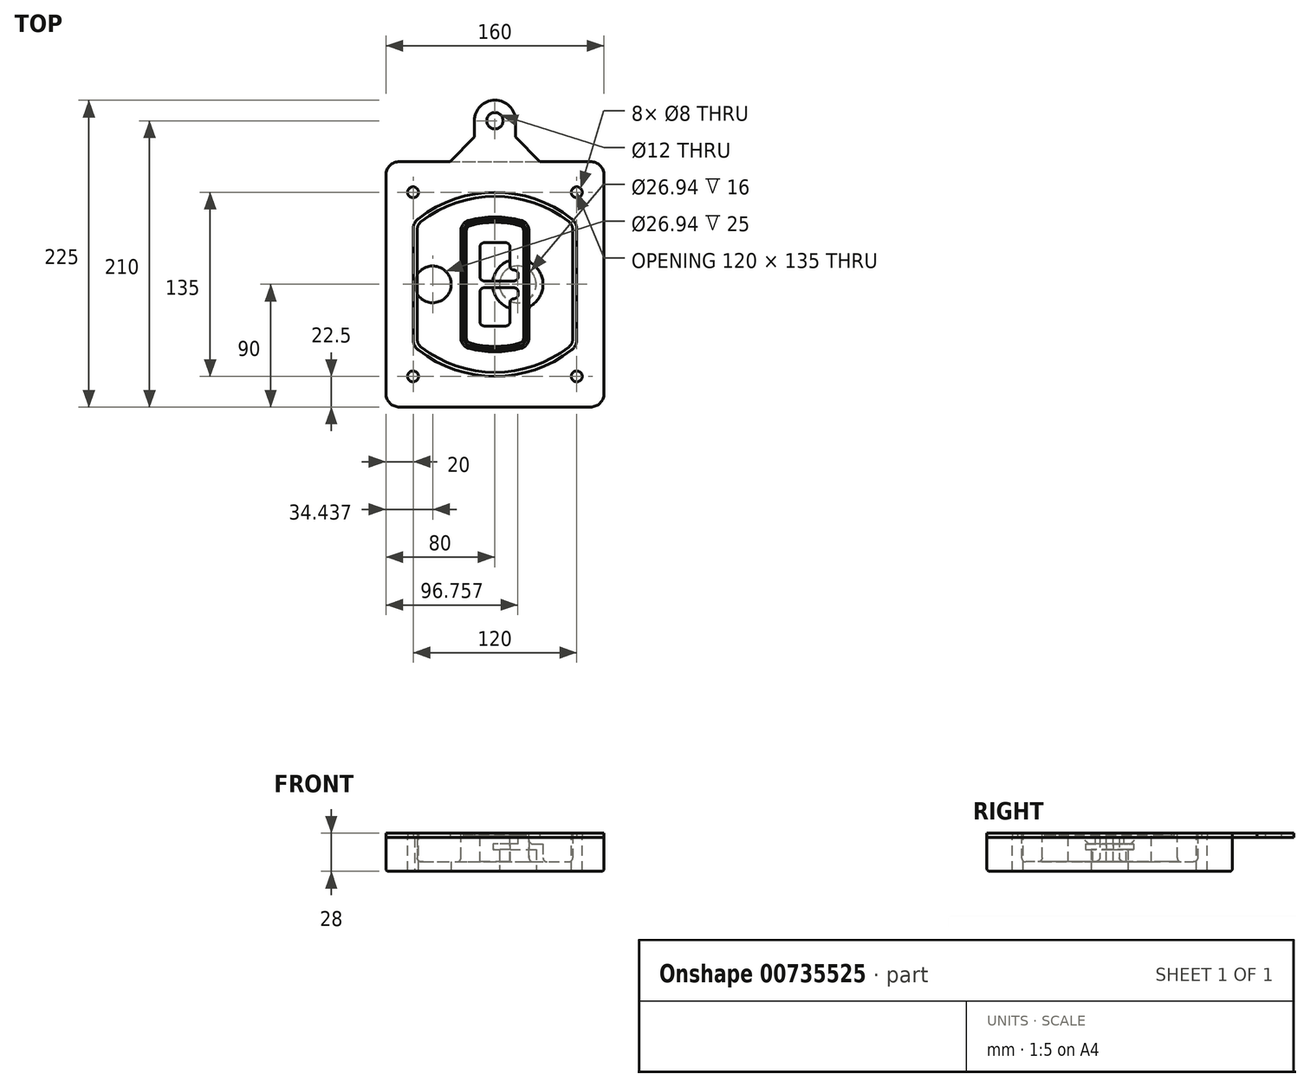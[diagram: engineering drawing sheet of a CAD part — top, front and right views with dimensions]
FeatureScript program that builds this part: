
annotation { "Feature Type Name" : "Feature", "Feature Type Description" : "" }
export const myFeature = defineFeature(function(context is Context, id is Id, definition is map)
    precondition{}
    {
        {
            var Q0;
            Q0=qCreatedBy(makeId("Top.planeOp"),FACE);
            var sketch = newSketch(context, id + "F0", { "sketchPlane" : qUnion([Q0])});
            skPoint(sketch, "E0.rect.middle", {"position": v(0, 0) * mm});
            skLineSegment(sketch, "E1.bottom", {"start": v(-70, -90) * mm, "end": v(70, -90) * mm});
            skLineSegment(sketch, "E1.top", {"start": v(-70, 90) * mm, "end": v(70, 90) * mm});
            skLineSegment(sketch, "E1.left", {"start": v(-80, -80) * mm, "end": v(-80, 80) * mm});
            skLineSegment(sketch, "E1.right", {"start": v(80, -80) * mm, "end": v(80, 80) * mm});
            skLineSegment(sketch, "E2", {"start": v(-80, 90) * mm, "end": v(80, -90) * mm, "construction": true});
            skLineSegment(sketch, "E3", {"start": v(80, 90) * mm, "end": v(-80, -90) * mm, "construction": true});
            skCircle(sketch, "E4", {"center": v(-60, 67.5) * mm, "radius": 4 * mm});
            skCircle(sketch, "E5", {"center": v(60, 67.5) * mm, "radius": 4 * mm});
            skCircle(sketch, "E6", {"center": v(60, -67.5) * mm, "radius": 4 * mm});
            skCircle(sketch, "E7", {"center": v(-60, -67.5) * mm, "radius": 4 * mm});
            skLineSegment(sketch, "E8", {"start": v(-60, 67.5) * mm, "end": v(60, 67.5) * mm, "construction": true});
            skLineSegment(sketch, "E9", {"start": v(60, 67.5) * mm, "end": v(60, -67.5) * mm, "construction": true});
            skLineSegment(sketch, "E10", {"start": v(60, -67.5) * mm, "end": v(-60, -67.5) * mm, "construction": true});
            skLineSegment(sketch, "E11", {"start": v(-60, -67.5) * mm, "end": v(-60, 67.5) * mm, "construction": true});
            skLineSegment(sketch, "E12", {"start": v(-60, 40.3) * mm, "end": v(-60, -40.3) * mm});
            skLineSegment(sketch, "E13", {"start": v(60, 40.3) * mm, "end": v(60, -40.3) * mm});
            skArc(sketch, "E14", {"start": v(56.15, 48.18) * mm, "mid": v(0, 67.5) * mm, "end": v(-56.15, 48.18) * mm});
            skArc(sketch, "E15", {"start": v(-56.15, -48.18) * mm, "mid": v(0, -67.5) * mm, "end": v(56.15, -48.18) * mm});
            skLineSegment(sketch, "E16", {"start": v(-60, 0) * mm, "end": v(60, 0) * mm, "construction": true});
            skPoint(sketch, "E17.visualSharp", {"position": v(-60, -45) * mm});
            skArc(sketch, "E17.filletArc", {"start": v(-60, -40.3) * mm, "mid": v(-58.99, -44.68) * mm, "end": v(-56.15, -48.18) * mm});
            skPoint(sketch, "E18.visualSharp", {"position": v(-60, 45) * mm});
            skArc(sketch, "E18.filletArc", {"start": v(-56.15, 48.18) * mm, "mid": v(-58.99, 44.68) * mm, "end": v(-60, 40.3) * mm});
            skPoint(sketch, "E19.visualSharp", {"position": v(60, 45) * mm});
            skArc(sketch, "E19.filletArc", {"start": v(60, 40.3) * mm, "mid": v(58.99, 44.68) * mm, "end": v(56.15, 48.18) * mm});
            skPoint(sketch, "E20.visualSharp", {"position": v(60, -45) * mm});
            skArc(sketch, "E20.filletArc", {"start": v(56.15, -48.18) * mm, "mid": v(58.99, -44.68) * mm, "end": v(60, -40.3) * mm});
            skPoint(sketch, "E21.visualSharp", {"position": v(-80, 90) * mm});
            skArc(sketch, "E21.filletArc", {"start": v(-70, 90) * mm, "mid": v(-77.07, 87.07) * mm, "end": v(-80, 80) * mm});
            skPoint(sketch, "E22.visualSharp", {"position": v(80, 90) * mm});
            skArc(sketch, "E22.filletArc", {"start": v(80, 80) * mm, "mid": v(77.07, 87.07) * mm, "end": v(70, 90) * mm});
            skPoint(sketch, "E23.visualSharp", {"position": v(80, -90) * mm});
            skArc(sketch, "E23.filletArc", {"start": v(70, -90) * mm, "mid": v(77.07, -87.07) * mm, "end": v(80, -80) * mm});
            skPoint(sketch, "E24.visualSharp", {"position": v(-80, -90) * mm});
            skArc(sketch, "E24.filletArc", {"start": v(-80, -80) * mm, "mid": v(-77.07, -87.07) * mm, "end": v(-70, -90) * mm});
            skArc(sketch, "E25.0", {"start": v(57, 40.3) * mm, "mid": v(56.3, 43.36) * mm, "end": v(54.3, 45.81) * mm});
            skLineSegment(sketch, "E25.1", {"start": v(57, 40.3) * mm, "end": v(57, -40.3) * mm});
            skArc(sketch, "E25.2", {"start": v(54.3, -45.81) * mm, "mid": v(56.3, -43.36) * mm, "end": v(57, -40.3) * mm});
            skArc(sketch, "E25.3", {"start": v(-54.3, -45.81) * mm, "mid": v(0, -64.5) * mm, "end": v(54.3, -45.81) * mm});
            skArc(sketch, "E25.4", {"start": v(-57, -40.3) * mm, "mid": v(-56.3, -43.36) * mm, "end": v(-54.3, -45.81) * mm});
            skArc(sketch, "E25.5", {"start": v(54.3, 45.81) * mm, "mid": v(0, 64.5) * mm, "end": v(-54.3, 45.81) * mm});
            skLineSegment(sketch, "E25.6", {"start": v(-57, 40.3) * mm, "end": v(-57, -40.3) * mm});
            skArc(sketch, "E25.7", {"start": v(-54.3, 45.81) * mm, "mid": v(-56.3, 43.36) * mm, "end": v(-57, 40.3) * mm});
            skArc(sketch, "E26.0", {"start": v(-58.62, 51.33) * mm, "mid": v(-62.58, 46.43) * mm, "end": v(-64, 40.3) * mm});
            skArc(sketch, "E26.1", {"start": v(58.62, 51.33) * mm, "mid": v(0, 71.5) * mm, "end": v(-58.62, 51.33) * mm});
            skArc(sketch, "E26.2", {"start": v(64, 40.3) * mm, "mid": v(62.58, 46.43) * mm, "end": v(58.62, 51.33) * mm});
            skLineSegment(sketch, "E26.3", {"start": v(64, 40.3) * mm, "end": v(64, -40.3) * mm});
            skArc(sketch, "E26.4", {"start": v(58.62, -51.33) * mm, "mid": v(62.58, -46.43) * mm, "end": v(64, -40.3) * mm});
            skLineSegment(sketch, "E26.5", {"start": v(-64, 40.3) * mm, "end": v(-64, -40.3) * mm});
            skArc(sketch, "E26.6", {"start": v(-58.62, -51.33) * mm, "mid": v(0, -71.5) * mm, "end": v(58.62, -51.33) * mm});
            skArc(sketch, "E26.7", {"start": v(-64, -40.3) * mm, "mid": v(-62.58, -46.43) * mm, "end": v(-58.62, -51.33) * mm});
            skSolve(sketch);
        }
        {
            var Q0;
            Q0=makeQuery(id+"F0.imprint","IMPRINT",FACE,{"disambiguationData":[TD([[makeQuery(id+"F0.imprint","IMPRINT",EDGE,{"derivedFrom":sQuery(id+"F0.wireOp",EDGE,"E1.bottom")}),1.0]])]});
            var Q1;
            Q1=makeQuery(id+"F0.imprint","IMPRINT",FACE,{"disambiguationData":[TD([[makeQuery(id+"F0.imprint","IMPRINT",EDGE,{"derivedFrom":sQuery(id+"F0.wireOp",EDGE,"E12")}),1.0]])]});
            var Q2;
            Q2=makeQuery(id+"F0.imprint","IMPRINT",FACE,{"disambiguationData":[TD([[makeQuery(id+"F0.imprint","IMPRINT",EDGE,{"derivedFrom":sQuery(id+"F0.wireOp",EDGE,"E25.0")}),1.0]])]});
            var Q3;
            Q3=makeQuery(id+"F0.imprint","IMPRINT",FACE,{"disambiguationData":[TD([[makeQuery(id+"F0.imprint","IMPRINT",EDGE,{"derivedFrom":sQuery(id+"F0.wireOp",EDGE,"E12")}),-1.0]])]});
            extrude(context, id + "F1", {"entities" : qUnion([Q0, Q1, Q2, Q3]), "oppositeDirection" : true, "depth" : 25 * mm, "offsetDistance" : 25 * mm});
        }
        {
            var Q0;
            Q0=makeQuery(id+"F0.imprint","IMPRINT",FACE,{"disambiguationData":[TD([[makeQuery(id+"F0.imprint","IMPRINT",EDGE,{"derivedFrom":sQuery(id+"F0.wireOp",EDGE,"E12")}),1.0]])]});
            extrude(context, id + "F2", {"entities" : qUnion([Q0]), "operationType" : NewBodyOperationType.ADD, "depth" : 3 * mm});
        }
        {
            var Q0;
            Q0=makeQuery(id+"F0.imprint","IMPRINT",FACE,{"disambiguationData":[TD([[makeQuery(id+"F0.imprint","IMPRINT",EDGE,{"derivedFrom":sQuery(id+"F0.wireOp",EDGE,"E25.0")}),1.0]])]});
            extrude(context, id + "F3", {"entities" : qUnion([Q0]), "operationType" : NewBodyOperationType.REMOVE, "oppositeDirection" : true, "depth" : 18 * mm});
        }
        {
            var Q0;
            Q0=makeQuery(id+"F2.opExtrude","CAP_FACE",FACE,{"disambiguationData":[OSD([sQuery(id+"F0.wireOp",EDGE,"E12"),sQuery(id+"F0.wireOp",EDGE,"E13"),sQuery(id+"F0.wireOp",EDGE,"E14"),sQuery(id+"F0.wireOp",EDGE,"E15"),sQuery(id+"F0.wireOp",EDGE,"E17.filletArc"),sQuery(id+"F0.wireOp",EDGE,"E18.filletArc"),sQuery(id+"F0.wireOp",EDGE,"E19.filletArc"),sQuery(id+"F0.wireOp",EDGE,"E20.filletArc"),sQuery(id+"F0.wireOp",EDGE,"E25.0"),sQuery(id+"F0.wireOp",EDGE,"E25.1"),sQuery(id+"F0.wireOp",EDGE,"E25.2"),sQuery(id+"F0.wireOp",EDGE,"E25.3"),sQuery(id+"F0.wireOp",EDGE,"E25.4"),sQuery(id+"F0.wireOp",EDGE,"E25.5"),sQuery(id+"F0.wireOp",EDGE,"E25.6"),sQuery(id+"F0.wireOp",EDGE,"E25.7")])],"isStart":false});
            var sketch = newSketch(context, id + "F4", { "sketchPlane" : qUnion([Q0])});
            skArc(sketch, "E27.0", {"start": v(-19.08, -46.97) * mm, "mid": v(0, -49.5) * mm, "end": v(19.08, -46.97) * mm});
            skArc(sketch, "E28.0", {"start": v(19.08, 46.97) * mm, "mid": v(0, 49.5) * mm, "end": v(-19.08, 46.97) * mm});
            skLineSegment(sketch, "E29", {"start": v(-25, 39.25) * mm, "end": v(-25, -39.25) * mm});
            skLineSegment(sketch, "E30", {"start": v(25, 39.25) * mm, "end": v(25, -39.25) * mm});
            skLineSegment(sketch, "E31", {"start": v(-25, 45.1) * mm, "end": v(25, 45.1) * mm, "construction": true});
            skLineSegment(sketch, "E32", {"start": v(-25, -45.1) * mm, "end": v(25, -45.1) * mm, "construction": true});
            skPoint(sketch, "E33.visualSharp", {"position": v(-25, 45.1) * mm});
            skArc(sketch, "E33.filletArc", {"start": v(-19.08, 46.97) * mm, "mid": v(-23.35, 44.11) * mm, "end": v(-25, 39.25) * mm});
            skPoint(sketch, "E34.visualSharp", {"position": v(25, 45.1) * mm});
            skArc(sketch, "E34.filletArc", {"start": v(25, 39.25) * mm, "mid": v(23.35, 44.11) * mm, "end": v(19.08, 46.97) * mm});
            skPoint(sketch, "E35.visualSharp", {"position": v(25, -45.1) * mm});
            skArc(sketch, "E35.filletArc", {"start": v(19.08, -46.97) * mm, "mid": v(23.35, -44.11) * mm, "end": v(25, -39.25) * mm});
            skPoint(sketch, "E36.visualSharp", {"position": v(-25, -45.1) * mm});
            skArc(sketch, "E36.filletArc", {"start": v(-25, -39.25) * mm, "mid": v(-23.35, -44.11) * mm, "end": v(-19.08, -46.97) * mm});
            skArc(sketch, "E37.0", {"start": v(54.3, 45.81) * mm, "mid": v(0, 64.5) * mm, "end": v(-54.3, 45.81) * mm});
            skArc(sketch, "E37.1", {"start": v(-54.3, 45.81) * mm, "mid": v(-56.3, 43.36) * mm, "end": v(-57, 40.3) * mm});
            skLineSegment(sketch, "E37.2", {"start": v(-57, 40.3) * mm, "end": v(-57, -40.3) * mm});
            skArc(sketch, "E37.3", {"start": v(-57, -40.3) * mm, "mid": v(-56.3, -43.36) * mm, "end": v(-54.3, -45.81) * mm});
            skArc(sketch, "E37.4", {"start": v(-54.3, -45.81) * mm, "mid": v(0, -64.5) * mm, "end": v(54.3, -45.81) * mm});
            skArc(sketch, "E37.5", {"start": v(54.3, -45.81) * mm, "mid": v(56.3, -43.36) * mm, "end": v(57, -40.3) * mm});
            skLineSegment(sketch, "E37.6", {"start": v(57, 40.3) * mm, "end": v(57, -40.3) * mm});
            skArc(sketch, "E37.7", {"start": v(57, 40.3) * mm, "mid": v(56.3, 43.36) * mm, "end": v(54.3, 45.81) * mm});
            skLineSegment(sketch, "E38.0", {"start": v(23, 39.25) * mm, "end": v(23, -39.25) * mm});
            skArc(sketch, "E38.1", {"start": v(18.56, -45.04) * mm, "mid": v(21.76, -42.9) * mm, "end": v(23, -39.25) * mm});
            skArc(sketch, "E38.2", {"start": v(-18.56, -45.04) * mm, "mid": v(0, -47.5) * mm, "end": v(18.56, -45.04) * mm});
            skArc(sketch, "E38.3", {"start": v(-23, -39.25) * mm, "mid": v(-21.76, -42.9) * mm, "end": v(-18.56, -45.04) * mm});
            skLineSegment(sketch, "E38.4", {"start": v(-23, 39.25) * mm, "end": v(-23, -39.25) * mm});
            skArc(sketch, "E38.5", {"start": v(23, 39.25) * mm, "mid": v(21.76, 42.9) * mm, "end": v(18.56, 45.04) * mm});
            skArc(sketch, "E38.6", {"start": v(-18.56, 45.04) * mm, "mid": v(-21.76, 42.9) * mm, "end": v(-23, 39.25) * mm});
            skArc(sketch, "E38.7", {"start": v(18.56, 45.04) * mm, "mid": v(0, 47.5) * mm, "end": v(-18.56, 45.04) * mm});
            skArc(sketch, "E39.0", {"start": v(21, 39.25) * mm, "mid": v(20.18, 41.68) * mm, "end": v(18.04, 43.1) * mm});
            skLineSegment(sketch, "E39.1", {"start": v(21, 39.25) * mm, "end": v(21, -39.25) * mm});
            skArc(sketch, "E39.2", {"start": v(18.04, -43.1) * mm, "mid": v(20.18, -41.68) * mm, "end": v(21, -39.25) * mm});
            skArc(sketch, "E39.3", {"start": v(-18.04, -43.1) * mm, "mid": v(0, -45.5) * mm, "end": v(18.04, -43.1) * mm});
            skArc(sketch, "E39.4", {"start": v(-21, -39.25) * mm, "mid": v(-20.18, -41.68) * mm, "end": v(-18.04, -43.1) * mm});
            skArc(sketch, "E39.5", {"start": v(18.04, 43.1) * mm, "mid": v(0, 45.5) * mm, "end": v(-18.04, 43.1) * mm});
            skLineSegment(sketch, "E39.6", {"start": v(-21, 39.25) * mm, "end": v(-21, -39.25) * mm});
            skArc(sketch, "E39.7", {"start": v(-18.04, 43.1) * mm, "mid": v(-20.18, 41.68) * mm, "end": v(-21, 39.25) * mm});
            skLineSegment(sketch, "E40", {"start": v(-25, 0) * mm, "end": v(25, 0) * mm, "construction": true});
            skLineSegment(sketch, "E41", {"start": v(-11, 5.5) * mm, "end": v(-11, 27.5) * mm});
            skLineSegment(sketch, "E42", {"start": v(-8, 30.5) * mm, "end": v(8, 30.5) * mm});
            skLineSegment(sketch, "E43", {"start": v(11, 27.5) * mm, "end": v(11, 13.5) * mm});
            skLineSegment(sketch, "E44", {"start": v(14, 10.5) * mm, "end": v(14, 10.5) * mm});
            skLineSegment(sketch, "E45", {"start": v(17, 7.5) * mm, "end": v(17, 5.5) * mm});
            skLineSegment(sketch, "E46", {"start": v(14, 2.5) * mm, "end": v(-8, 2.5) * mm});
            skPoint(sketch, "E47.visualSharp", {"position": v(-11, 30.5) * mm});
            skArc(sketch, "E47.filletArc", {"start": v(-8, 30.5) * mm, "mid": v(-10.12, 29.62) * mm, "end": v(-11, 27.5) * mm});
            skPoint(sketch, "E48.visualSharp", {"position": v(11, 30.5) * mm});
            skArc(sketch, "E48.filletArc", {"start": v(11, 27.5) * mm, "mid": v(10.12, 29.62) * mm, "end": v(8, 30.5) * mm});
            skPoint(sketch, "E49.visualSharp", {"position": v(11, 10.5) * mm});
            skArc(sketch, "E49.filletArc", {"start": v(11, 13.5) * mm, "mid": v(11.88, 11.38) * mm, "end": v(14, 10.5) * mm});
            skPoint(sketch, "E50.visualSharp", {"position": v(17, 10.5) * mm});
            skArc(sketch, "E50.filletArc", {"start": v(17, 7.5) * mm, "mid": v(16.12, 9.62) * mm, "end": v(14, 10.5) * mm});
            skPoint(sketch, "E51.visualSharp", {"position": v(17, 2.5) * mm});
            skArc(sketch, "E51.filletArc", {"start": v(14, 2.5) * mm, "mid": v(16.12, 3.38) * mm, "end": v(17, 5.5) * mm});
            skPoint(sketch, "E52.visualSharp", {"position": v(-11, 2.5) * mm});
            skArc(sketch, "E52.filletArc", {"start": v(-11, 5.5) * mm, "mid": v(-10.12, 3.38) * mm, "end": v(-8, 2.5) * mm});
            skLineSegment(sketch, "E53.0.MirrorCS", {"start": v(14, -2.5) * mm, "end": v(-8, -2.5) * mm});
            skArc(sketch, "E54.0.MirrorCS", {"start": v(-11, -5.5) * mm, "mid": v(-10.12, -3.38) * mm, "end": v(-8, -2.5) * mm});
            skLineSegment(sketch, "E55.0.MirrorCS", {"start": v(-11, -5.5) * mm, "end": v(-11, -27.5) * mm});
            skArc(sketch, "E56.0.MirrorCS", {"start": v(-8, -30.5) * mm, "mid": v(-10.12, -29.62) * mm, "end": v(-11, -27.5) * mm});
            skLineSegment(sketch, "E57.0.MirrorCS", {"start": v(-8, -30.5) * mm, "end": v(8, -30.5) * mm});
            skArc(sketch, "E58.0.MirrorCS", {"start": v(11, -27.5) * mm, "mid": v(10.12, -29.62) * mm, "end": v(8, -30.5) * mm});
            skLineSegment(sketch, "E59.0.MirrorCS", {"start": v(11, -27.5) * mm, "end": v(11, -13.5) * mm});
            skArc(sketch, "E60.0.MirrorCS", {"start": v(11, -13.5) * mm, "mid": v(11.88, -11.38) * mm, "end": v(14, -10.5) * mm});
            skArc(sketch, "E61.0.MirrorCS", {"start": v(17, -7.5) * mm, "mid": v(16.12, -9.62) * mm, "end": v(14, -10.5) * mm});
            skLineSegment(sketch, "E62.0.MirrorCS", {"start": v(17, -7.5) * mm, "end": v(17, -5.5) * mm});
            skArc(sketch, "E63.0.MirrorCS", {"start": v(14, -2.5) * mm, "mid": v(16.12, -3.38) * mm, "end": v(17, -5.5) * mm});
            skSolve(sketch);
        }
        {
            var Q0;
            Q0=makeQuery(id+"F4.imprint","IMPRINT",FACE,{"disambiguationData":[TD([[makeQuery(id+"F4.imprint","IMPRINT",EDGE,{"derivedFrom":sQuery(id+"F4.wireOp",EDGE,"E27.0")}),1.0]])]});
            var Q1;
            Q1=makeQuery(id+"F4.imprint","IMPRINT",FACE,{"disambiguationData":[TD([[makeQuery(id+"F4.imprint","IMPRINT",EDGE,{"derivedFrom":sQuery(id+"F4.wireOp",EDGE,"E38.0")}),-1.0]])]});
            var Q2;
            Q2=makeQuery(id+"F4.imprint","IMPRINT",FACE,{"disambiguationData":[TD([[makeQuery(id+"F4.imprint","IMPRINT",EDGE,{"derivedFrom":sQuery(id+"F4.wireOp",EDGE,"E39.0")}),1.0]])]});
            extrude(context, id + "F5", {"entities" : qUnion([Q0, Q1, Q2]), "operationType" : NewBodyOperationType.ADD, "endBound" : BoundingType.UP_TO_NEXT, "oppositeDirection" : true, "depth" : 25 * mm});
        }
        {
            var Q0;
            Q0=makeQuery(id+"F4.imprint","IMPRINT",FACE,{"disambiguationData":[TD([[makeQuery(id+"F4.imprint","IMPRINT",EDGE,{"derivedFrom":sQuery(id+"F4.wireOp",EDGE,"E38.0")}),-1.0]])]});
            extrude(context, id + "F6", {"entities" : qUnion([Q0]), "operationType" : NewBodyOperationType.REMOVE, "oppositeDirection" : true, "depth" : 2 * mm});
        }
        {
            var Q0;
            Q0=makeQuery(id+"F1.opExtrude","CAP_FACE",FACE,{"disambiguationData":[OSD([sQuery(id+"F0.wireOp",EDGE,"E1.bottom"),sQuery(id+"F0.wireOp",EDGE,"E1.top"),sQuery(id+"F0.wireOp",EDGE,"E1.left"),sQuery(id+"F0.wireOp",EDGE,"E1.right"),sQuery(id+"F0.wireOp",EDGE,"E4"),sQuery(id+"F0.wireOp",EDGE,"E5"),sQuery(id+"F0.wireOp",EDGE,"E6"),sQuery(id+"F0.wireOp",EDGE,"E7"),sQuery(id+"F0.wireOp",EDGE,"E21.filletArc"),sQuery(id+"F0.wireOp",EDGE,"E22.filletArc"),sQuery(id+"F0.wireOp",EDGE,"E23.filletArc"),sQuery(id+"F0.wireOp",EDGE,"E24.filletArc")])],"isStart":false});
            var sketch = newSketch(context, id + "F7", { "sketchPlane" : qUnion([Q0])});
            skCircle(sketch, "E64", {"center": v(16.76, 0) * mm, "radius": 13.47 * mm});
            skCircle(sketch, "E65", {"center": v(-45.56, 0) * mm, "radius": 13.47 * mm});
            skLineSegment(sketch, "E66", {"start": v(80, 0) * mm, "end": v(-80, 0) * mm});
            skCircle(sketch, "E67", {"center": v(16.76, 0) * mm, "radius": 18.47 * mm});
            skCircle(sketch, "E68", {"center": v(60, -67.5) * mm, "radius": 6 * mm});
            skCircle(sketch, "E69", {"center": v(-60, -67.5) * mm, "radius": 6 * mm});
            skCircle(sketch, "E70", {"center": v(-60, 67.5) * mm, "radius": 6 * mm});
            skCircle(sketch, "E71", {"center": v(60, 67.5) * mm, "radius": 6 * mm});
            skSolve(sketch);
        }
        {
            var Q0;
            {var subQ1=sQuery(id+"F7.wireOp",EDGE,"E66");var subQ4=sQuery(id+"F7.wireOp",EDGE,"E64");var subQ6=makeQuery(id+"F7.imprint","INTERSECT",VERTEX,{"disambiguationData":[OD(0.0)],"derivedFrom":[subQ4,subQ1]});Q0=makeQuery(id+"F7.imprint","IMPRINT",FACE,{"disambiguationData":[TD([[makeQuery(id+"F7.imprint","IMPRINT",EDGE,{"disambiguationData":[TD([[subQ6,-1.0]])],"derivedFrom":subQ4}),-1.0]])]});}
            var Q1;
            {var subQ0=sQuery(id+"F7.wireOp",EDGE,"E66");var subQ1=sQuery(id+"F7.wireOp",EDGE,"E64");var subQ3=makeQuery(id+"F7.imprint","INTERSECT",VERTEX,{"disambiguationData":[OD(0.0)],"derivedFrom":[subQ1,subQ0]});Q1=makeQuery(id+"F7.imprint","IMPRINT",FACE,{"disambiguationData":[TD([[makeQuery(id+"F7.imprint","IMPRINT",EDGE,{"disambiguationData":[TD([[subQ3,-1.0]])],"derivedFrom":subQ1}),1.0]])]});}
            var Q2;
            {var subQ0=sQuery(id+"F7.wireOp",EDGE,"E66");var subQ1=sQuery(id+"F7.wireOp",EDGE,"E64");var subQ3=makeQuery(id+"F7.imprint","INTERSECT",VERTEX,{"disambiguationData":[OD(0.0)],"derivedFrom":[subQ1,subQ0]});Q2=makeQuery(id+"F7.imprint","IMPRINT",FACE,{"disambiguationData":[TD([[makeQuery(id+"F7.imprint","IMPRINT",EDGE,{"disambiguationData":[TD([[subQ3,1.0]])],"derivedFrom":subQ1}),1.0]])]});}
            var Q3;
            {var subQ1=sQuery(id+"F7.wireOp",EDGE,"E66");var subQ4=sQuery(id+"F7.wireOp",EDGE,"E64");var subQ6=makeQuery(id+"F7.imprint","INTERSECT",VERTEX,{"disambiguationData":[OD(0.0)],"derivedFrom":[subQ4,subQ1]});Q3=makeQuery(id+"F7.imprint","IMPRINT",FACE,{"disambiguationData":[TD([[makeQuery(id+"F7.imprint","IMPRINT",EDGE,{"disambiguationData":[TD([[subQ6,1.0]])],"derivedFrom":subQ4}),-1.0]])]});}
            extrude(context, id + "F8", {"entities" : qUnion([Q0, Q1, Q2, Q3]), "operationType" : NewBodyOperationType.ADD, "oppositeDirection" : true, "depth" : 20 * mm});
        }
        {
            var Q0;
            {var subQ0=sQuery(id+"F7.wireOp",EDGE,"E66");var subQ1=sQuery(id+"F7.wireOp",EDGE,"E64");var subQ3=makeQuery(id+"F7.imprint","INTERSECT",VERTEX,{"disambiguationData":[OD(0.0)],"derivedFrom":[subQ1,subQ0]});Q0=makeQuery(id+"F7.imprint","IMPRINT",FACE,{"disambiguationData":[TD([[makeQuery(id+"F7.imprint","IMPRINT",EDGE,{"disambiguationData":[TD([[subQ3,-1.0]])],"derivedFrom":subQ1}),1.0]])]});}
            var Q1;
            {var subQ0=sQuery(id+"F7.wireOp",EDGE,"E66");var subQ1=sQuery(id+"F7.wireOp",EDGE,"E64");var subQ3=makeQuery(id+"F7.imprint","INTERSECT",VERTEX,{"disambiguationData":[OD(0.0)],"derivedFrom":[subQ1,subQ0]});Q1=makeQuery(id+"F7.imprint","IMPRINT",FACE,{"disambiguationData":[TD([[makeQuery(id+"F7.imprint","IMPRINT",EDGE,{"disambiguationData":[TD([[subQ3,1.0]])],"derivedFrom":subQ1}),1.0]])]});}
            extrude(context, id + "F9", {"entities" : qUnion([Q0, Q1]), "operationType" : NewBodyOperationType.REMOVE, "oppositeDirection" : true, "depth" : 16 * mm});
        }
        {
            var Q0;
            Q0=makeQuery(id+"F9.boolean.opBoolean","COPY",FACE,{"derivedFrom":makeQuery(id+"F9.opExtrude","CAP_FACE",FACE,{"disambiguationData":[OSD([sQuery(id+"F7.wireOp",EDGE,"E64")])],"isStart":false})});
            var sketch = newSketch(context, id + "F10", { "sketchPlane" : qUnion([Q0])});
            skArc(sketch, "E72.0", {"start": v(11, 17.55) * mm, "mid": v(2.57, 11.82) * mm, "end": v(-1.54, 2.5) * mm});
            skArc(sketch, "E72.1", {"start": v(-1.54, -2.5) * mm, "mid": v(2.57, -11.82) * mm, "end": v(11, -17.55) * mm});
            skLineSegment(sketch, "E73", {"start": v(-1.54, -2.5) * mm, "end": v(14, -2.5) * mm});
            skLineSegment(sketch, "E74.0", {"start": v(14, 2.5) * mm, "end": v(-1.54, 2.5) * mm});
            skArc(sketch, "E74.1", {"start": v(14, 2.5) * mm, "mid": v(16.12, 3.38) * mm, "end": v(17, 5.5) * mm});
            skLineSegment(sketch, "E74.2", {"start": v(17, 7.5) * mm, "end": v(17, 5.5) * mm});
            skArc(sketch, "E74.3", {"start": v(17, 7.5) * mm, "mid": v(16.12, 9.62) * mm, "end": v(14, 10.5) * mm});
            skArc(sketch, "E74.4", {"start": v(11, 13.5) * mm, "mid": v(11.88, 11.38) * mm, "end": v(14, 10.5) * mm});
            skLineSegment(sketch, "E74.5", {"start": v(11, 17.55) * mm, "end": v(11, 13.5) * mm});
            skLineSegment(sketch, "E74.7", {"start": v(14, -2.5) * mm, "end": v(-1.54, -2.5) * mm});
            skArc(sketch, "E74.8", {"start": v(14, -2.5) * mm, "mid": v(16.12, -3.38) * mm, "end": v(17, -5.5) * mm});
            skLineSegment(sketch, "E74.9", {"start": v(17, -7.5) * mm, "end": v(17, -5.5) * mm});
            skArc(sketch, "E74.10", {"start": v(17, -7.5) * mm, "mid": v(16.12, -9.62) * mm, "end": v(14, -10.5) * mm});
            skArc(sketch, "E74.11", {"start": v(11, -13.5) * mm, "mid": v(11.88, -11.38) * mm, "end": v(14, -10.5) * mm});
            skLineSegment(sketch, "E74.12", {"start": v(11, -17.55) * mm, "end": v(11, -13.5) * mm});
            skPoint(sketch, "E75.orphan", {"position": v(11, -27.5) * mm});
            skPoint(sketch, "E76.orphan", {"position": v(-8, -2.5) * mm});
            skPoint(sketch, "E77.orphan", {"position": v(-8, 2.5) * mm});
            skPoint(sketch, "E78.orphan", {"position": v(11, 27.5) * mm});
            skSolve(sketch);
        }
        {
            var Q0;
            {var subQ7=sQuery(id+"F10.wireOp",EDGE,"E72.0");var subQ14=sQuery(id+"F10.wireOp",EDGE,"E72.1");var subQ16=sQuery(id+"F10.wireOp",EDGE,"E74.1");var subQ18=sQuery(id+"F10.wireOp",EDGE,"E74.8");Q0=qUnion([makeQuery(id+"F10.imprint","IMPRINT",FACE,{"disambiguationData":[TD([[makeQuery(id+"F10.imprint","IMPRINT",EDGE,{"derivedFrom":subQ7}),1.0]])]}),makeQuery(id+"F10.imprint","IMPRINT",FACE,{"disambiguationData":[TD([[makeQuery(id+"F10.imprint","IMPRINT",EDGE,{"derivedFrom":subQ14}),1.0]])]}),makeQuery(id+"F10.imprint","IMPRINT",FACE,{"disambiguationData":[TD([[makeQuery(id+"F10.imprint","IMPRINT",EDGE,{"derivedFrom":subQ16}),1.0]])]}),makeQuery(id+"F10.imprint","IMPRINT",FACE,{"disambiguationData":[TD([[makeQuery(id+"F10.imprint","IMPRINT",EDGE,{"derivedFrom":subQ18}),-1.0]])]})]);}
            var Q1;
            Q1=makeQuery(id+"F5.boolean.opBoolean","SPLIT",FACE,{"disambiguationData":[TD([makeQuery(id+"F5.opExtrude","SWEPT_FACE",FACE,{"disambiguationData":[OSD([sQuery(id+"F4.wireOp",EDGE,"E41")])]})])],"derivedFrom":makeQuery(id+"F3.boolean.opBoolean","COPY",FACE,{"derivedFrom":makeQuery(id+"F3.opExtrude","CAP_FACE",FACE,{"disambiguationData":[OSD([sQuery(id+"F0.wireOp",EDGE,"E25.0"),sQuery(id+"F0.wireOp",EDGE,"E25.1"),sQuery(id+"F0.wireOp",EDGE,"E25.2"),sQuery(id+"F0.wireOp",EDGE,"E25.3"),sQuery(id+"F0.wireOp",EDGE,"E25.4"),sQuery(id+"F0.wireOp",EDGE,"E25.5"),sQuery(id+"F0.wireOp",EDGE,"E25.6"),sQuery(id+"F0.wireOp",EDGE,"E25.7")])],"isStart":false})})});
            extrude(context, id + "F11", {"entities" : qUnion([Q0]), "operationType" : NewBodyOperationType.REMOVE, "endBound" : BoundingType.UP_TO_SURFACE, "endBoundEntityFace" : qUnion([Q1]), "depth" : 25 * mm});
        }
        {
            var Q0;
            {var subQ0=sQuery(id+"F7.wireOp",EDGE,"E66");var subQ1=sQuery(id+"F7.wireOp",EDGE,"E65");var subQ3=makeQuery(id+"F7.imprint","INTERSECT",VERTEX,{"disambiguationData":[OD(0.0)],"derivedFrom":[subQ1,subQ0]});Q0=makeQuery(id+"F7.imprint","IMPRINT",FACE,{"disambiguationData":[TD([[makeQuery(id+"F7.imprint","IMPRINT",EDGE,{"disambiguationData":[TD([[subQ3,-1.0]])],"derivedFrom":subQ1}),1.0]])]});}
            var Q1;
            {var subQ0=sQuery(id+"F7.wireOp",EDGE,"E66");var subQ1=sQuery(id+"F7.wireOp",EDGE,"E65");var subQ3=makeQuery(id+"F7.imprint","INTERSECT",VERTEX,{"disambiguationData":[OD(0.0)],"derivedFrom":[subQ1,subQ0]});Q1=makeQuery(id+"F7.imprint","IMPRINT",FACE,{"disambiguationData":[TD([[makeQuery(id+"F7.imprint","IMPRINT",EDGE,{"disambiguationData":[TD([[subQ3,1.0]])],"derivedFrom":subQ1}),1.0]])]});}
            extrude(context, id + "F12", {"entities" : qUnion([Q0, Q1]), "operationType" : NewBodyOperationType.REMOVE, "oppositeDirection" : true, "depth" : 25 * mm});
        }
        {
            var Q0;
            Q0=makeQuery(id+"F3.boolean.opBoolean","COPY",EDGE,{"derivedFrom":makeQuery(id+"F3.opExtrude","CAP_EDGE",EDGE,{"disambiguationData":[OSD([sQuery(id+"F0.wireOp",EDGE,"E25.6")])],"isStart":false})});
            var Q1;
            Q1=makeQuery(id+"F8.boolean.opBoolean","INTERSECT",EDGE,{"derivedFrom":[makeQuery(id+"F5.opExtrude","SWEPT_FACE",FACE,{"disambiguationData":[OSD([sQuery(id+"F4.wireOp",EDGE,"E30")])]}),makeQuery(id+"F8.opExtrude","CAP_FACE",FACE,{"disambiguationData":[OSD([sQuery(id+"F7.wireOp",EDGE,"E67")])],"isStart":false})]});
            var Q2;
            Q2=makeQuery(id+"F8.boolean.opBoolean","INTERSECT",EDGE,{"disambiguationData":[OD(1.0)],"derivedFrom":[makeQuery(id+"F5.opExtrude","SWEPT_FACE",FACE,{"disambiguationData":[OSD([sQuery(id+"F4.wireOp",EDGE,"E30")])]}),makeQuery(id+"F8.opExtrude","SWEPT_FACE",FACE,{"disambiguationData":[OSD([sQuery(id+"F7.wireOp",EDGE,"E67")])]})]});
            var Q3;
            {var subQ0=sQuery(id+"F4.wireOp",EDGE,"E30");Q3=makeQuery(id+"F8.boolean.opBoolean","SPLIT",EDGE,{"disambiguationData":[TD([makeQuery(id+"F5.opExtrude","SWEPT_FACE",FACE,{"disambiguationData":[OSD([sQuery(id+"F4.wireOp",EDGE,"E35.filletArc")])]})])],"derivedFrom":makeQuery(id+"F5.opExtrude","CAP_EDGE",EDGE,{"disambiguationData":[OSD([subQ0])],"isStart":false})});}
            var Q4;
            {var subQ0=sQuery(id+"F0.wireOp",EDGE,"E25.7");var subQ1=sQuery(id+"F0.wireOp",EDGE,"E25.1");var subQ2=sQuery(id+"F0.wireOp",EDGE,"E25.6");var subQ3=sQuery(id+"F0.wireOp",EDGE,"E25.5");var subQ4=sQuery(id+"F0.wireOp",EDGE,"E25.4");var subQ5=sQuery(id+"F0.wireOp",EDGE,"E25.0");var subQ6=sQuery(id+"F0.wireOp",EDGE,"E25.2");var subQ7=sQuery(id+"F0.wireOp",EDGE,"E25.3");Q4=makeQuery(id+"F8.boolean.opBoolean","INTERSECT",EDGE,{"derivedFrom":[makeQuery(id+"F5.boolean.opBoolean","SPLIT",FACE,{"disambiguationData":[TD([makeQuery(id+"F2.opExtrude","SWEPT_FACE",FACE,{"disambiguationData":[OSD([subQ5])]})])],"derivedFrom":makeQuery(id+"F3.boolean.opBoolean","COPY",FACE,{"derivedFrom":makeQuery(id+"F3.opExtrude","CAP_FACE",FACE,{"disambiguationData":[OSD([subQ5,subQ1,subQ6,subQ7,subQ4,subQ3,subQ2,subQ0])],"isStart":false})})}),makeQuery(id+"F8.opExtrude","SWEPT_FACE",FACE,{"disambiguationData":[OSD([sQuery(id+"F7.wireOp",EDGE,"E67")])]})]});}
            var Q5;
            Q5=makeQuery(id+"F8.boolean.opBoolean","INTERSECT",EDGE,{"disambiguationData":[OD(0.0)],"derivedFrom":[makeQuery(id+"F5.opExtrude","SWEPT_FACE",FACE,{"disambiguationData":[OSD([sQuery(id+"F4.wireOp",EDGE,"E30")])]}),makeQuery(id+"F8.opExtrude","SWEPT_FACE",FACE,{"disambiguationData":[OSD([sQuery(id+"F7.wireOp",EDGE,"E67")])]})]});
            fillet(context, id + "F13", {"entities" : qUnion([Q0, Q1, Q2, Q3, Q4, Q5]), "radius" : 3 * mm, "tangentPropagation" : true, "allowEdgeOverflow" : false});
        }
        {
            var Q0;
            Q0=makeQuery(id+"F1.opExtrude","CAP_EDGE",EDGE,{"disambiguationData":[OSD([sQuery(id+"F0.wireOp",EDGE,"E1.bottom")])],"isStart":false});
            fillet(context, id + "F14", {"entities" : qUnion([Q0]), "radius" : 2 * mm, "tangentPropagation" : true, "allowEdgeOverflow" : false});
        }
        {
            var Q0;
            {var subQ0=sQuery(id+"F0.wireOp",EDGE,"E21.filletArc");var subQ1=sQuery(id+"F0.wireOp",EDGE,"E7");var subQ2=sQuery(id+"F0.wireOp",EDGE,"E6");var subQ3=sQuery(id+"F0.wireOp",EDGE,"E5");var subQ4=sQuery(id+"F0.wireOp",EDGE,"E4");var subQ5=sQuery(id+"F0.wireOp",EDGE,"E22.filletArc");var subQ6=sQuery(id+"F0.wireOp",EDGE,"E1.bottom");var subQ7=sQuery(id+"F0.wireOp",EDGE,"E1.right");var subQ8=sQuery(id+"F0.wireOp",EDGE,"E1.top");var subQ9=sQuery(id+"F0.wireOp",EDGE,"E1.left");var subQ10=sQuery(id+"F0.wireOp",EDGE,"E23.filletArc");var subQ11=sQuery(id+"F0.wireOp",EDGE,"E24.filletArc");Q0=makeQuery(id+"F2.boolean.opBoolean","SPLIT",FACE,{"disambiguationData":[TD([makeQuery(id+"F1.opExtrude","SWEPT_FACE",FACE,{"disambiguationData":[OSD([subQ6])]})])],"derivedFrom":makeQuery(id+"F1.opExtrude","CAP_FACE",FACE,{"disambiguationData":[OSD([subQ6,subQ8,subQ9,subQ7,subQ4,subQ3,subQ2,subQ1,subQ0,subQ5,subQ10,subQ11])],"isStart":true})});}
            var sketch = newSketch(context, id + "F15", { "sketchPlane" : qUnion([Q0])});
            skLineSegment(sketch, "E79", {"start": v(0, 90) * mm, "end": v(0, 120) * mm, "construction": true});
            skCircle(sketch, "E80", {"center": v(0, 120) * mm, "radius": 6 * mm});
            skLineSegment(sketch, "E81", {"start": v(-33, 90) * mm, "end": v(-15, 108) * mm});
            skLineSegment(sketch, "E82", {"start": v(33, 90) * mm, "end": v(15, 108) * mm});
            skLineSegment(sketch, "E83", {"start": v(-15, 108) * mm, "end": v(-15, 120) * mm});
            skArc(sketch, "E84", {"start": v(15, 120) * mm, "mid": v(0, 135) * mm, "end": v(-15, 120) * mm});
            skLineSegment(sketch, "E85", {"start": v(15, 108) * mm, "end": v(15, 120) * mm});
            skLineSegment(sketch, "E86", {"start": v(-80, 0) * mm, "end": v(80, 0) * mm, "construction": true});
            skArc(sketch, "E87.MirrorCS", {"start": v(15, -120) * mm, "mid": v(0, -135) * mm, "end": v(-15, -120) * mm});
            skLineSegment(sketch, "E88.MirrorCS", {"start": v(15, -108) * mm, "end": v(15, -120) * mm});
            skLineSegment(sketch, "E89.MirrorCS", {"start": v(33, -90) * mm, "end": v(15, -108) * mm});
            skLineSegment(sketch, "E90.MirrorCS", {"start": v(-33, -90) * mm, "end": v(-15, -108) * mm});
            skLineSegment(sketch, "E91.MirrorCS", {"start": v(-15, -108) * mm, "end": v(-15, -120) * mm});
            skLineSegment(sketch, "E92.MirrorCS", {"start": v(0, -90) * mm, "end": v(0, -120) * mm, "construction": true});
            skCircle(sketch, "E93.MirrorC", {"center": v(0, -120) * mm, "radius": 6 * mm});
            skSolve(sketch);
        }
        {
            var Q0;
            Q0=makeQuery(id+"F15.imprint","IMPRINT",FACE,{"disambiguationData":[TD([[makeQuery(id+"F15.imprint","IMPRINT",EDGE,{"derivedFrom":sQuery(id+"F15.wireOp",EDGE,"E80")}),-1.0]])]});
            var Q1;
            Q1=makeQuery(id+"F15.imprint","IMPRINT",FACE,{"disambiguationData":[TD([[makeQuery(id+"F15.imprint","IMPRINT",EDGE,{"derivedFrom":makeQuery(id+"F1.opExtrude","CAP_EDGE",EDGE,{"disambiguationData":[OSD([sQuery(id+"F0.wireOp",EDGE,"E1.left")])],"isStart":true})}),-1.0]])]});
            var Q2;
            Q2=makeQuery(id+"F15.imprint","IMPRINT",FACE,{"disambiguationData":[TD([[makeQuery(id+"F15.imprint","IMPRINT",EDGE,{"derivedFrom":sQuery(id+"F15.wireOp",EDGE,"E87.MirrorCS")}),-1.0]])]});
            var Q3;
            Q3=makeQuery(id+"F2.opExtrude","CAP_FACE",FACE,{"disambiguationData":[OSD([sQuery(id+"F0.wireOp",EDGE,"E12"),sQuery(id+"F0.wireOp",EDGE,"E13"),sQuery(id+"F0.wireOp",EDGE,"E14"),sQuery(id+"F0.wireOp",EDGE,"E15"),sQuery(id+"F0.wireOp",EDGE,"E17.filletArc"),sQuery(id+"F0.wireOp",EDGE,"E18.filletArc"),sQuery(id+"F0.wireOp",EDGE,"E19.filletArc"),sQuery(id+"F0.wireOp",EDGE,"E20.filletArc"),sQuery(id+"F0.wireOp",EDGE,"E25.0"),sQuery(id+"F0.wireOp",EDGE,"E25.1"),sQuery(id+"F0.wireOp",EDGE,"E25.2"),sQuery(id+"F0.wireOp",EDGE,"E25.3"),sQuery(id+"F0.wireOp",EDGE,"E25.4"),sQuery(id+"F0.wireOp",EDGE,"E25.5"),sQuery(id+"F0.wireOp",EDGE,"E25.6"),sQuery(id+"F0.wireOp",EDGE,"E25.7")])],"isStart":false});
            extrude(context, id + "F16", {"entities" : qUnion([Q0, Q1, Q2]), "endBound" : BoundingType.UP_TO_SURFACE, "depth" : 25 * mm, "endBoundEntityFace" : qUnion([Q3]), "offsetDistance" : 25 * mm});
        }
    });
